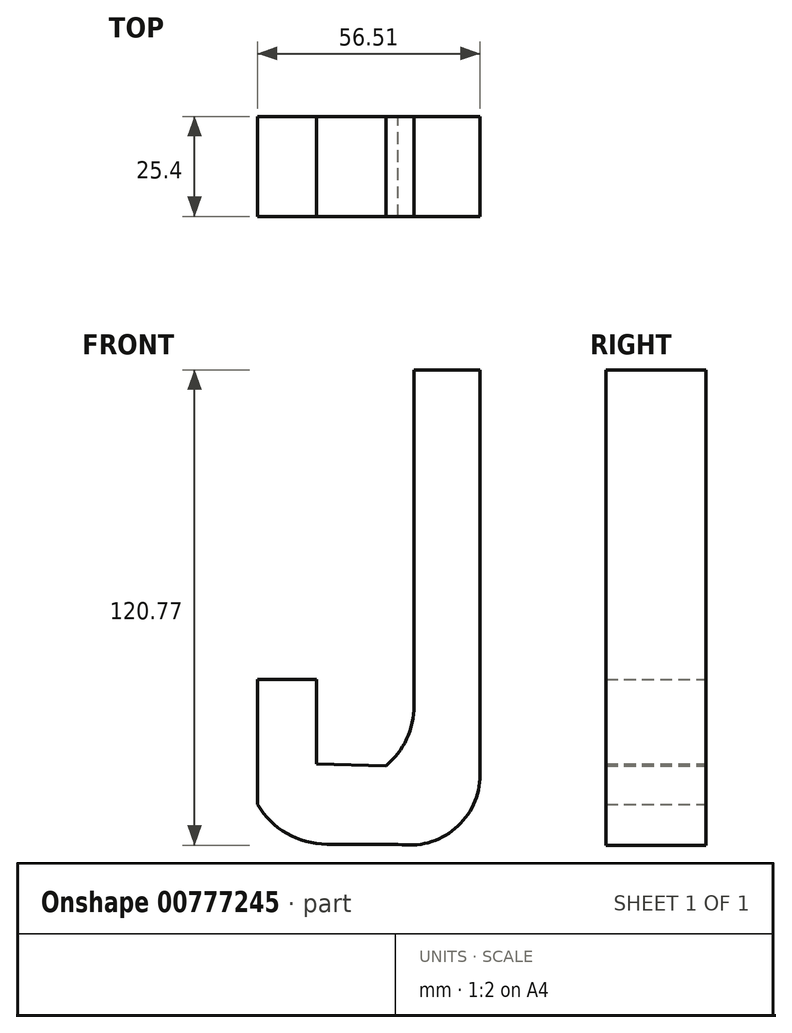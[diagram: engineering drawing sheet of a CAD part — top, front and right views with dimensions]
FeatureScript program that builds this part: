
annotation { "Feature Type Name" : "Feature", "Feature Type Description" : "" }
export const myFeature = defineFeature(function(context is Context, id is Id, definition is map)
    precondition{}
    {
        {
            var Q0;
            Q0=qCreatedBy(makeId("Front.planeOp"),FACE);
            var sketch = newSketch(context, id + "F0", { "sketchPlane" : qUnion([Q0])});
            skLineSegment(sketch, "E0", {"start": v(20.83, 52.11) * mm, "end": v(20.83, -50.82) * mm});
            skLineSegment(sketch, "E1", {"start": v(20.83, 52.11) * mm, "end": v(4.1, 52.11) * mm});
            skArc(sketch, "E2", {"start": v(0, -68.4) * mm, "mid": v(14.5, -64.45) * mm, "end": v(20.83, -50.82) * mm});
            skLineSegment(sketch, "E3", {"start": v(0, -68.4) * mm, "end": v(-18.1, -68.4) * mm});
            skArc(sketch, "E4", {"start": v(-35.68, -58.31) * mm, "mid": v(-28.23, -65.7) * mm, "end": v(-18.1, -68.4) * mm});
            skLineSegment(sketch, "E5", {"start": v(-35.68, -58.31) * mm, "end": v(-35.68, -26.6) * mm});
            skLineSegment(sketch, "E6", {"start": v(-20.69, -26.6) * mm, "end": v(-35.68, -26.6) * mm});
            skLineSegment(sketch, "E7", {"start": v(-20.69, -26.6) * mm, "end": v(-20.69, -48.03) * mm});
            skLineSegment(sketch, "E8", {"start": v(4.1, 52.11) * mm, "end": v(4.1, -33.23) * mm});
            skArc(sketch, "E9", {"start": v(-3.1, -48.51) * mm, "mid": v(2.22, -41.68) * mm, "end": v(4.1, -33.23) * mm});
            skLineSegment(sketch, "E10", {"start": v(-20.69, -48.03) * mm, "end": v(-3.1, -48.51) * mm});
            skSolve(sketch);
        }
        {
            var Q0;
            Q0 = qSketchRegion(id + "F0", true);
            extrude(context, id + "F1", {"entities" : qUnion([Q0]), "depth" : 25.4 * mm, "offsetDistance" : 25.4 * mm});
        }
    });
